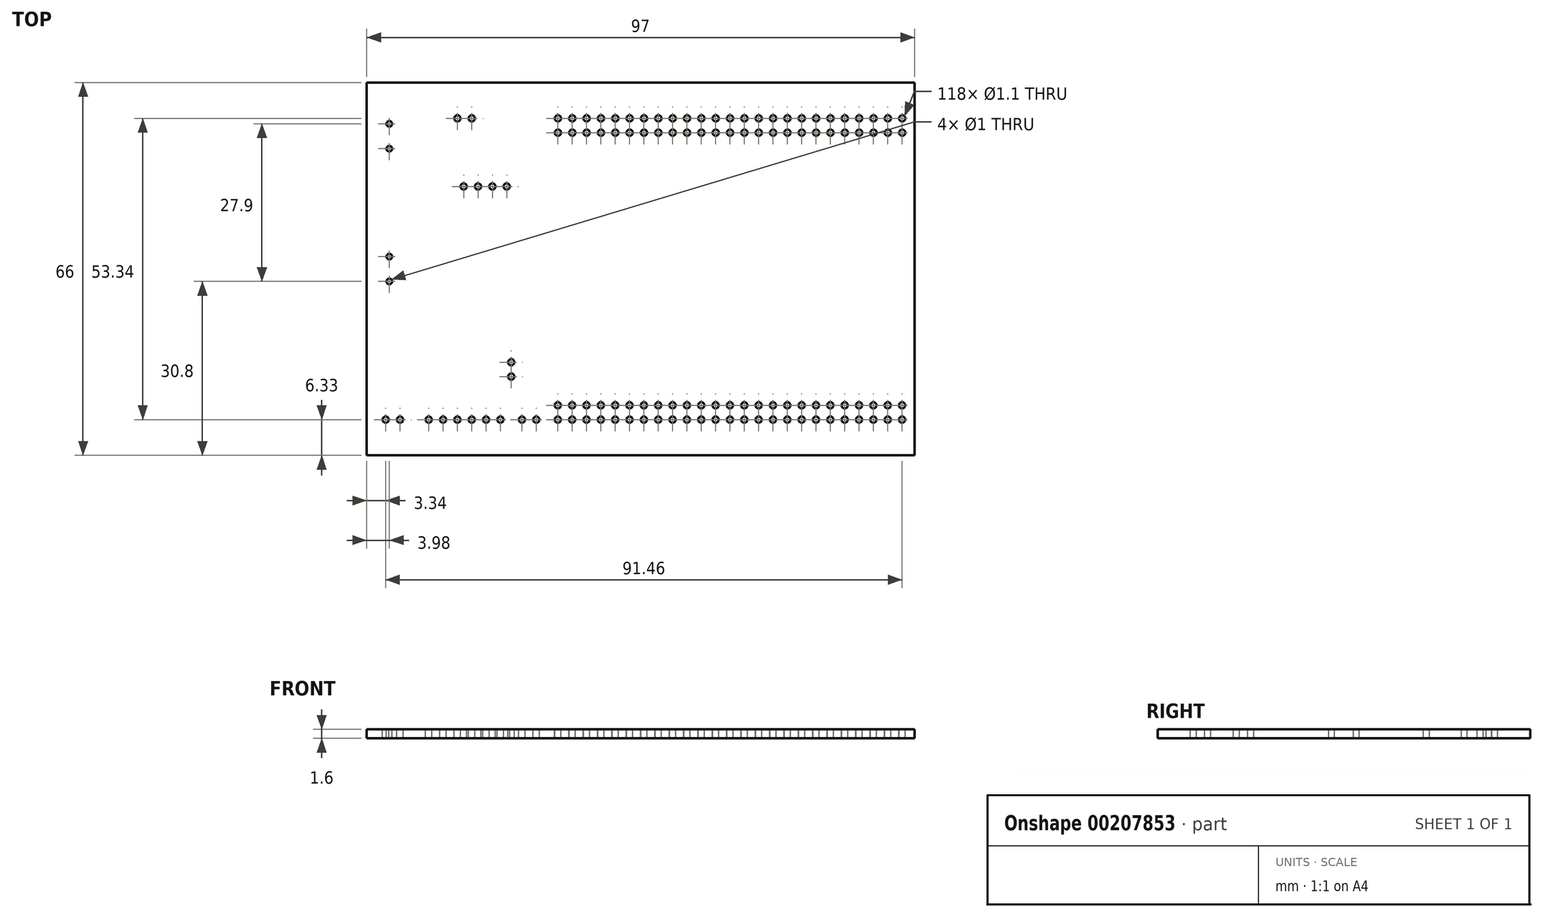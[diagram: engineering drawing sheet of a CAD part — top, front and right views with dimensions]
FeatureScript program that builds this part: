
annotation { "Feature Type Name" : "Feature", "Feature Type Description" : "" }
export const myFeature = defineFeature(function(context is Context, id is Id, definition is map)
    precondition{}
    {
        {
            var Q0;
            Q0=qCreatedBy(makeId("Top.planeOp"),FACE);
            var sketch = newSketch(context, id + "F0", { "sketchPlane" : qUnion([Q0])});
            skLineSegment(sketch, "E0.bottom", {"start": v(-66.5, 32) * mm, "end": v(30.5, 32) * mm});
            skLineSegment(sketch, "E0.top", {"start": v(-66.5, -34) * mm, "end": v(30.5, -34) * mm});
            skLineSegment(sketch, "E0.left", {"start": v(-66.5, 32) * mm, "end": v(-66.5, -34) * mm});
            skLineSegment(sketch, "E0.right", {"start": v(30.5, 32) * mm, "end": v(30.5, -34) * mm});
            skSolve(sketch);
        }
        {
            var Q0;
            Q0 = qSketchRegion(id + "F0", true);
            extrude(context, id + "F1", {"entities" : qUnion([Q0]), "oppositeDirection" : true, "depth" : 1.6 * mm});
        }
        {
            var Q0;
            Q0=qCreatedBy(makeId("Top.planeOp"),FACE);
            var sketch = newSketch(context, id + "F2", { "sketchPlane" : qUnion([Q0])});
            skCircle(sketch, "E1", {"center": v(28.28, -27.67) * mm, "radius": 0.55 * mm});
            skCircle(sketch, "E2.0.1.0", {"center": v(28.28, -25.13) * mm, "radius": 0.55 * mm});
            skCircle(sketch, "E2.1.0.0", {"center": v(25.74, -27.67) * mm, "radius": 0.55 * mm});
            skCircle(sketch, "E2.1.1.0", {"center": v(25.74, -25.13) * mm, "radius": 0.55 * mm});
            skCircle(sketch, "E2.2.0.0", {"center": v(23.2, -27.67) * mm, "radius": 0.55 * mm});
            skCircle(sketch, "E2.2.1.0", {"center": v(23.2, -25.13) * mm, "radius": 0.55 * mm});
            skCircle(sketch, "E2.3.0.0", {"center": v(20.66, -27.67) * mm, "radius": 0.55 * mm});
            skCircle(sketch, "E2.3.1.0", {"center": v(20.66, -25.13) * mm, "radius": 0.55 * mm});
            skCircle(sketch, "E2.4.0.0", {"center": v(18.12, -27.67) * mm, "radius": 0.55 * mm});
            skCircle(sketch, "E2.4.1.0", {"center": v(18.12, -25.13) * mm, "radius": 0.55 * mm});
            skCircle(sketch, "E2.5.0.0", {"center": v(15.58, -27.67) * mm, "radius": 0.55 * mm});
            skCircle(sketch, "E2.5.1.0", {"center": v(15.58, -25.13) * mm, "radius": 0.55 * mm});
            skCircle(sketch, "E2.6.0.0", {"center": v(13.04, -27.67) * mm, "radius": 0.55 * mm});
            skCircle(sketch, "E2.6.1.0", {"center": v(13.04, -25.13) * mm, "radius": 0.55 * mm});
            skCircle(sketch, "E2.7.0.0", {"center": v(10.5, -27.67) * mm, "radius": 0.55 * mm});
            skCircle(sketch, "E2.7.1.0", {"center": v(10.5, -25.13) * mm, "radius": 0.55 * mm});
            skCircle(sketch, "E2.8.0.0", {"center": v(7.96, -27.67) * mm, "radius": 0.55 * mm});
            skCircle(sketch, "E2.8.1.0", {"center": v(7.96, -25.13) * mm, "radius": 0.55 * mm});
            skCircle(sketch, "E2.9.0.0", {"center": v(5.42, -27.67) * mm, "radius": 0.55 * mm});
            skCircle(sketch, "E2.9.1.0", {"center": v(5.42, -25.13) * mm, "radius": 0.55 * mm});
            skCircle(sketch, "E2.10.0.0", {"center": v(2.88, -27.67) * mm, "radius": 0.55 * mm});
            skCircle(sketch, "E2.10.1.0", {"center": v(2.88, -25.13) * mm, "radius": 0.55 * mm});
            skCircle(sketch, "E2.11.0.0", {"center": v(0.34, -27.67) * mm, "radius": 0.55 * mm});
            skCircle(sketch, "E2.11.1.0", {"center": v(0.34, -25.13) * mm, "radius": 0.55 * mm});
            skCircle(sketch, "E2.12.0.0", {"center": v(-2.2, -27.67) * mm, "radius": 0.55 * mm});
            skCircle(sketch, "E2.12.1.0", {"center": v(-2.2, -25.13) * mm, "radius": 0.55 * mm});
            skCircle(sketch, "E2.13.0.0", {"center": v(-4.74, -27.67) * mm, "radius": 0.55 * mm});
            skCircle(sketch, "E2.13.1.0", {"center": v(-4.74, -25.13) * mm, "radius": 0.55 * mm});
            skCircle(sketch, "E2.14.0.0", {"center": v(-7.28, -27.67) * mm, "radius": 0.55 * mm});
            skCircle(sketch, "E2.14.1.0", {"center": v(-7.28, -25.13) * mm, "radius": 0.55 * mm});
            skCircle(sketch, "E2.15.0.0", {"center": v(-9.82, -27.67) * mm, "radius": 0.55 * mm});
            skCircle(sketch, "E2.15.1.0", {"center": v(-9.82, -25.13) * mm, "radius": 0.55 * mm});
            skCircle(sketch, "E2.16.0.0", {"center": v(-12.36, -27.67) * mm, "radius": 0.55 * mm});
            skCircle(sketch, "E2.16.1.0", {"center": v(-12.36, -25.13) * mm, "radius": 0.55 * mm});
            skCircle(sketch, "E2.17.0.0", {"center": v(-14.9, -27.67) * mm, "radius": 0.55 * mm});
            skCircle(sketch, "E2.17.1.0", {"center": v(-14.9, -25.13) * mm, "radius": 0.55 * mm});
            skCircle(sketch, "E2.18.0.0", {"center": v(-17.44, -27.67) * mm, "radius": 0.55 * mm});
            skCircle(sketch, "E2.18.1.0", {"center": v(-17.44, -25.13) * mm, "radius": 0.55 * mm});
            skCircle(sketch, "E2.19.0.0", {"center": v(-19.98, -27.67) * mm, "radius": 0.55 * mm});
            skCircle(sketch, "E2.19.1.0", {"center": v(-19.98, -25.13) * mm, "radius": 0.55 * mm});
            skLineSegment(sketch, "E2.direction1", {"start": v(28.28, -27.67) * mm, "end": v(25.74, -27.67) * mm, "construction": true});
            skLineSegment(sketch, "E2.direction2", {"start": v(28.28, -27.67) * mm, "end": v(28.28, -25.13) * mm, "construction": true});
            skCircle(sketch, "E3.0.20.0", {"center": v(-22.52, -27.67) * mm, "radius": 0.55 * mm});
            skCircle(sketch, "E3.0.20.1", {"center": v(-22.52, -25.13) * mm, "radius": 0.55 * mm});
            skCircle(sketch, "E3.0.21.0", {"center": v(-25.06, -27.67) * mm, "radius": 0.55 * mm});
            skCircle(sketch, "E3.0.21.1", {"center": v(-25.06, -25.13) * mm, "radius": 0.55 * mm});
            skCircle(sketch, "E3.0.22.0", {"center": v(-27.6, -27.67) * mm, "radius": 0.55 * mm});
            skCircle(sketch, "E3.0.22.1", {"center": v(-27.6, -25.13) * mm, "radius": 0.55 * mm});
            skCircle(sketch, "E3.0.23.0", {"center": v(-30.14, -27.67) * mm, "radius": 0.55 * mm});
            skCircle(sketch, "E3.0.23.1", {"center": v(-30.14, -25.13) * mm, "radius": 0.55 * mm});
            skCircle(sketch, "E3.0.24.0", {"center": v(-32.68, -27.67) * mm, "radius": 0.55 * mm});
            skCircle(sketch, "E3.0.24.1", {"center": v(-32.68, -25.13) * mm, "radius": 0.55 * mm});
            skCircle(sketch, "E4", {"center": v(28.3, 25.67) * mm, "radius": 0.55 * mm});
            skCircle(sketch, "E5", {"center": v(28.3, 23.13) * mm, "radius": 0.55 * mm});
            skCircle(sketch, "E6.1.0.0", {"center": v(25.76, 25.67) * mm, "radius": 0.55 * mm});
            skCircle(sketch, "E6.1.0.1", {"center": v(25.76, 23.13) * mm, "radius": 0.55 * mm});
            skCircle(sketch, "E6.2.0.0", {"center": v(23.22, 25.67) * mm, "radius": 0.55 * mm});
            skCircle(sketch, "E6.2.0.1", {"center": v(23.22, 23.13) * mm, "radius": 0.55 * mm});
            skCircle(sketch, "E6.3.0.0", {"center": v(20.68, 25.67) * mm, "radius": 0.55 * mm});
            skCircle(sketch, "E6.3.0.1", {"center": v(20.68, 23.13) * mm, "radius": 0.55 * mm});
            skCircle(sketch, "E6.4.0.0", {"center": v(18.14, 25.67) * mm, "radius": 0.55 * mm});
            skCircle(sketch, "E6.4.0.1", {"center": v(18.14, 23.13) * mm, "radius": 0.55 * mm});
            skCircle(sketch, "E6.5.0.0", {"center": v(15.6, 25.67) * mm, "radius": 0.55 * mm});
            skCircle(sketch, "E6.5.0.1", {"center": v(15.6, 23.13) * mm, "radius": 0.55 * mm});
            skCircle(sketch, "E6.6.0.0", {"center": v(13.06, 25.67) * mm, "radius": 0.55 * mm});
            skCircle(sketch, "E6.6.0.1", {"center": v(13.06, 23.13) * mm, "radius": 0.55 * mm});
            skCircle(sketch, "E6.7.0.0", {"center": v(10.52, 25.67) * mm, "radius": 0.55 * mm});
            skCircle(sketch, "E6.7.0.1", {"center": v(10.52, 23.13) * mm, "radius": 0.55 * mm});
            skCircle(sketch, "E6.8.0.0", {"center": v(7.98, 25.67) * mm, "radius": 0.55 * mm});
            skCircle(sketch, "E6.8.0.1", {"center": v(7.98, 23.13) * mm, "radius": 0.55 * mm});
            skCircle(sketch, "E6.9.0.0", {"center": v(5.44, 25.67) * mm, "radius": 0.55 * mm});
            skCircle(sketch, "E6.9.0.1", {"center": v(5.44, 23.13) * mm, "radius": 0.55 * mm});
            skCircle(sketch, "E6.10.0.0", {"center": v(2.9, 25.67) * mm, "radius": 0.55 * mm});
            skCircle(sketch, "E6.10.0.1", {"center": v(2.9, 23.13) * mm, "radius": 0.55 * mm});
            skCircle(sketch, "E6.11.0.0", {"center": v(0.36, 25.67) * mm, "radius": 0.55 * mm});
            skCircle(sketch, "E6.11.0.1", {"center": v(0.36, 23.13) * mm, "radius": 0.55 * mm});
            skCircle(sketch, "E6.12.0.0", {"center": v(-2.18, 25.67) * mm, "radius": 0.55 * mm});
            skCircle(sketch, "E6.12.0.1", {"center": v(-2.18, 23.13) * mm, "radius": 0.55 * mm});
            skCircle(sketch, "E6.13.0.0", {"center": v(-4.72, 25.67) * mm, "radius": 0.55 * mm});
            skCircle(sketch, "E6.13.0.1", {"center": v(-4.72, 23.13) * mm, "radius": 0.55 * mm});
            skCircle(sketch, "E6.14.0.0", {"center": v(-7.26, 25.67) * mm, "radius": 0.55 * mm});
            skCircle(sketch, "E6.14.0.1", {"center": v(-7.26, 23.13) * mm, "radius": 0.55 * mm});
            skCircle(sketch, "E6.15.0.0", {"center": v(-9.8, 25.67) * mm, "radius": 0.55 * mm});
            skCircle(sketch, "E6.15.0.1", {"center": v(-9.8, 23.13) * mm, "radius": 0.55 * mm});
            skCircle(sketch, "E6.16.0.0", {"center": v(-12.34, 25.67) * mm, "radius": 0.55 * mm});
            skCircle(sketch, "E6.16.0.1", {"center": v(-12.34, 23.13) * mm, "radius": 0.55 * mm});
            skCircle(sketch, "E6.17.0.0", {"center": v(-14.88, 25.67) * mm, "radius": 0.55 * mm});
            skCircle(sketch, "E6.17.0.1", {"center": v(-14.88, 23.13) * mm, "radius": 0.55 * mm});
            skCircle(sketch, "E6.18.0.0", {"center": v(-17.42, 25.67) * mm, "radius": 0.55 * mm});
            skCircle(sketch, "E6.18.0.1", {"center": v(-17.42, 23.13) * mm, "radius": 0.55 * mm});
            skCircle(sketch, "E6.19.0.0", {"center": v(-19.96, 25.67) * mm, "radius": 0.55 * mm});
            skCircle(sketch, "E6.19.0.1", {"center": v(-19.96, 23.13) * mm, "radius": 0.55 * mm});
            skCircle(sketch, "E6.20.0.0", {"center": v(-22.5, 25.67) * mm, "radius": 0.55 * mm});
            skCircle(sketch, "E6.20.0.1", {"center": v(-22.5, 23.13) * mm, "radius": 0.55 * mm});
            skCircle(sketch, "E6.21.0.0", {"center": v(-25.04, 25.67) * mm, "radius": 0.55 * mm});
            skCircle(sketch, "E6.21.0.1", {"center": v(-25.04, 23.13) * mm, "radius": 0.55 * mm});
            skCircle(sketch, "E6.22.0.0", {"center": v(-27.58, 25.67) * mm, "radius": 0.55 * mm});
            skCircle(sketch, "E6.22.0.1", {"center": v(-27.58, 23.13) * mm, "radius": 0.55 * mm});
            skCircle(sketch, "E6.23.0.0", {"center": v(-30.12, 25.67) * mm, "radius": 0.55 * mm});
            skCircle(sketch, "E6.23.0.1", {"center": v(-30.12, 23.13) * mm, "radius": 0.55 * mm});
            skCircle(sketch, "E6.24.0.0", {"center": v(-32.66, 25.67) * mm, "radius": 0.55 * mm});
            skCircle(sketch, "E6.24.0.1", {"center": v(-32.66, 23.13) * mm, "radius": 0.55 * mm});
            skLineSegment(sketch, "E6.direction1", {"start": v(28.3, 23.13) * mm, "end": v(25.76, 23.13) * mm, "construction": true});
            skSolve(sketch);
        }
        {
            var Q0;
            Q0 = qSketchRegion(id + "F2", true);
            extrude(context, id + "F3", {"entities" : qUnion([Q0]), "operationType" : NewBodyOperationType.REMOVE, "endBound" : BoundingType.THROUGH_ALL, "oppositeDirection" : true, "depth" : 25 * mm});
        }
        {
            var Q0;
            Q0=qCreatedBy(makeId("Top.planeOp"),FACE);
            var sketch = newSketch(context, id + "F4", { "sketchPlane" : qUnion([Q0])});
            skCircle(sketch, "E7", {"center": v(-63.16, -27.67) * mm, "radius": 0.55 * mm});
            skCircle(sketch, "E8", {"center": v(-60.62, -27.67) * mm, "radius": 0.55 * mm});
            skCircle(sketch, "E9", {"center": v(-50.46, 25.67) * mm, "radius": 0.55 * mm});
            skCircle(sketch, "E10", {"center": v(-47.92, 25.67) * mm, "radius": 0.55 * mm});
            skSolve(sketch);
        }
        {
            var Q0;
            Q0 = qSketchRegion(id + "F4", true);
            extrude(context, id + "F5", {"entities" : qUnion([Q0]), "operationType" : NewBodyOperationType.REMOVE, "endBound" : BoundingType.THROUGH_ALL, "oppositeDirection" : true, "depth" : 25 * mm});
        }
        {
            var Q0;
            Q0=qCreatedBy(makeId("Top.planeOp"),FACE);
            var sketch = newSketch(context, id + "F6", { "sketchPlane" : qUnion([Q0])});
            skCircle(sketch, "E11", {"center": v(-55.54, -27.67) * mm, "radius": 0.55 * mm});
            skCircle(sketch, "E12.1.0.0", {"center": v(-53, -27.67) * mm, "radius": 0.55 * mm});
            skCircle(sketch, "E12.2.0.0", {"center": v(-50.46, -27.67) * mm, "radius": 0.55 * mm});
            skCircle(sketch, "E12.3.0.0", {"center": v(-47.92, -27.67) * mm, "radius": 0.55 * mm});
            skCircle(sketch, "E12.4.0.0", {"center": v(-45.38, -27.67) * mm, "radius": 0.55 * mm});
            skCircle(sketch, "E12.5.0.0", {"center": v(-42.84, -27.67) * mm, "radius": 0.55 * mm});
            skLineSegment(sketch, "E12.direction1", {"start": v(-55.54, -27.67) * mm, "end": v(-53, -27.67) * mm, "construction": true});
            skSolve(sketch);
        }
        {
            var Q0;
            Q0 = qSketchRegion(id + "F6", true);
            extrude(context, id + "F7", {"entities" : qUnion([Q0]), "operationType" : NewBodyOperationType.REMOVE, "endBound" : BoundingType.THROUGH_ALL, "oppositeDirection" : true, "depth" : 25 * mm});
        }
        {
            var Q0;
            Q0=qCreatedBy(makeId("Top.planeOp"),FACE);
            var sketch = newSketch(context, id + "F8", { "sketchPlane" : qUnion([Q0])});
            skCircle(sketch, "E13", {"center": v(-40.93, -20.05) * mm, "radius": 0.55 * mm});
            skCircle(sketch, "E14", {"center": v(-49.35, 13.6) * mm, "radius": 0.55 * mm});
            skCircle(sketch, "E15.0.1.0", {"center": v(-40.93, -17.51) * mm, "radius": 0.55 * mm});
            skLineSegment(sketch, "E15.direction2", {"start": v(-40.93, -20.05) * mm, "end": v(-40.93, -17.51) * mm, "construction": true});
            skCircle(sketch, "E16.1.0.0", {"center": v(-46.81, 13.6) * mm, "radius": 0.55 * mm});
            skCircle(sketch, "E16.2.0.0", {"center": v(-44.27, 13.6) * mm, "radius": 0.55 * mm});
            skCircle(sketch, "E16.3.0.0", {"center": v(-41.73, 13.6) * mm, "radius": 0.55 * mm});
            skLineSegment(sketch, "E16.direction1", {"start": v(-49.35, 13.6) * mm, "end": v(-46.81, 13.6) * mm, "construction": true});
            skSolve(sketch);
        }
        {
            var Q0;
            Q0 = qSketchRegion(id + "F8", true);
            extrude(context, id + "F9", {"entities" : qUnion([Q0]), "operationType" : NewBodyOperationType.REMOVE, "endBound" : BoundingType.THROUGH_ALL, "oppositeDirection" : true, "depth" : 25 * mm});
        }
        {
            var Q0;
            Q0=qCreatedBy(makeId("Top.planeOp"),FACE);
            var sketch = newSketch(context, id + "F10", { "sketchPlane" : qUnion([Q0])});
            skCircle(sketch, "E17", {"center": v(-39.03, -27.67) * mm, "radius": 0.55 * mm});
            skCircle(sketch, "E18", {"center": v(-36.5, -27.67) * mm, "radius": 0.55 * mm});
            skSolve(sketch);
        }
        {
            var Q0;
            Q0 = qSketchRegion(id + "F10", true);
            extrude(context, id + "F11", {"entities" : qUnion([Q0]), "operationType" : NewBodyOperationType.REMOVE, "endBound" : BoundingType.THROUGH_ALL, "oppositeDirection" : true, "depth" : 25 * mm});
        }
        {
            var Q0;
            Q0=qCreatedBy(makeId("Top.planeOp"),FACE);
            var sketch = newSketch(context, id + "F12", { "sketchPlane" : qUnion([Q0])});
            skCircle(sketch, "E19", {"center": v(-62.52, 20.3) * mm, "radius": 0.5 * mm});
            skCircle(sketch, "E20", {"center": v(-62.52, 24.7) * mm, "radius": 0.5 * mm});
            skCircle(sketch, "E21", {"center": v(-62.52, 1.2) * mm, "radius": 0.5 * mm});
            skCircle(sketch, "E22", {"center": v(-62.52, -3.2) * mm, "radius": 0.5 * mm});
            skSolve(sketch);
        }
        {
            var Q0;
            Q0 = qSketchRegion(id + "F12", true);
            extrude(context, id + "F13", {"entities" : qUnion([Q0]), "operationType" : NewBodyOperationType.REMOVE, "endBound" : BoundingType.THROUGH_ALL, "oppositeDirection" : true, "depth" : 25 * mm});
        }
    });
